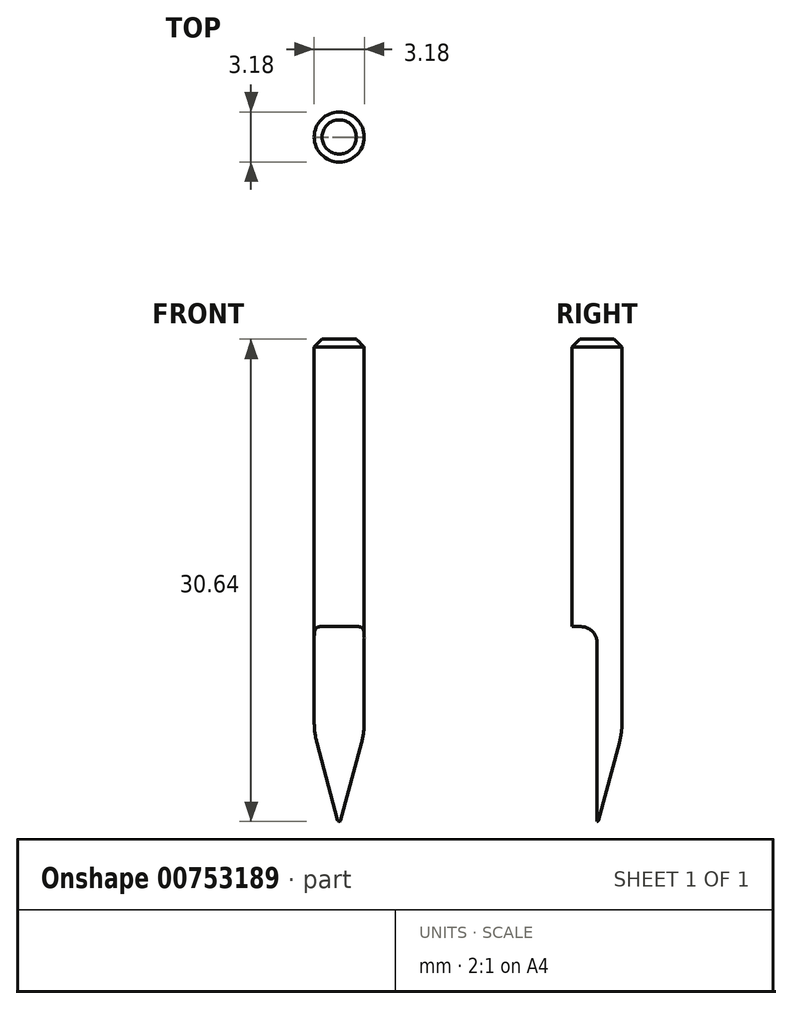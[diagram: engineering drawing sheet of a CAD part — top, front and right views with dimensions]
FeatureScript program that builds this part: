
annotation { "Feature Type Name" : "Feature", "Feature Type Description" : "" }
export const myFeature = defineFeature(function(context is Context, id is Id, definition is map)
    precondition{}
    {
        {
            var Q0;
            Q0=qCreatedBy(makeId("Top.planeOp"),FACE);
            var sketch = newSketch(context, id + "F0", { "sketchPlane" : qUnion([Q0])});
            skCircle(sketch, "E0", {"center": v(0, 0) * mm, "radius": 1.59 * mm});
            skSolve(sketch);
        }
        {
            var Q0;
            Q0=qSketchRegion(id+"F0",true);
            extrude(context, id + "F1", {"entities" : qUnion([Q0]), "depth" : 25 * mm, "offsetDistance" : 25 * mm});
        }
        {
            var Q0;
            Q0=qCreatedBy(makeId("Front.planeOp"),FACE);
            var sketch = newSketch(context, id + "F2", { "sketchPlane" : qUnion([Q0])});
            skLineSegment(sketch, "E1", {"start": v(0, 0) * mm, "end": v(-1.59, 0) * mm});
            skLineSegment(sketch, "E2", {"start": v(-1.59, 0) * mm, "end": v(-0.1, -5.56) * mm});
            skLineSegment(sketch, "E3", {"start": v(0, -5.64) * mm, "end": v(0, 0) * mm});
            skArc(sketch, "E4", {"start": v(-0.1, -5.56) * mm, "mid": v(-0.06, -5.62) * mm, "end": v(0, -5.64) * mm});
            skSolve(sketch);
        }
        {
            var Q0;
            Q0=qSketchRegion(id+"F2",true);
            var Q1;
            Q1=sQuery(id+"F2.wireOp",EDGE,"E3");
            revolve(context, id + "F3", {"operationType" : NewBodyOperationType.ADD, "entities" : qUnion([Q0]), "axis" : qUnion([Q1]), "revolveType" : RevolveType.FULL});
        }
        {
            var Q0;
            Q0=makeQuery(id+"F3.opRevolve","SWEPT_FACE",FACE,{"disambiguationData":[OSD([sQuery(id+"F2.wireOp",EDGE,"E2")])]});
            fillet(context, id + "F4", {"entities" : qUnion([Q0]), "radius" : 5 * mm, "tangentPropagation" : true, "allowEdgeOverflow" : false});
        }
        {
            var Q0;
            Q0=qCreatedBy(makeId("Right.planeOp"),FACE);
            var sketch = newSketch(context, id + "F5", { "sketchPlane" : qUnion([Q0])});
            skLineSegment(sketch, "E5.bottom", {"start": v(-1, 6.74) * mm, "end": v(-3.29, 6.74) * mm});
            skLineSegment(sketch, "E5.top", {"start": v(0, -6.52) * mm, "end": v(-3.29, -6.52) * mm});
            skLineSegment(sketch, "E5.left", {"start": v(0, 5.74) * mm, "end": v(0, -6.52) * mm});
            skLineSegment(sketch, "E5.right", {"start": v(-3.29, 6.74) * mm, "end": v(-3.29, -6.52) * mm});
            skPoint(sketch, "E6.visualSharp", {"position": v(0, 6.74) * mm});
            skArc(sketch, "E6.filletArc", {"start": v(0, 5.74) * mm, "mid": v(-0.3, 6.45) * mm, "end": v(-1, 6.74) * mm});
            skSolve(sketch);
        }
        {
            var Q0;
            Q0=qSketchRegion(id+"F5",true);
            extrude(context, id + "F6", {"entities" : qUnion([Q0]), "operationType" : NewBodyOperationType.REMOVE, "endBound" : BoundingType.SYMMETRIC, "oppositeDirection" : true, "depth" : 25 * mm, "offsetDistance" : 25 * mm});
        }
        {
            var Q0;
            Q0=makeQuery(id+"F1.opExtrude","CAP_EDGE",EDGE,{"disambiguationData":[OSD([sQuery(id+"F0.wireOp",EDGE,"E0")])],"isStart":false});
            chamfer(context, id + "F7", {"entities" : qUnion([Q0]), "width" : 0.5 * mm, "tangentPropagation" : true});
        }
    });
